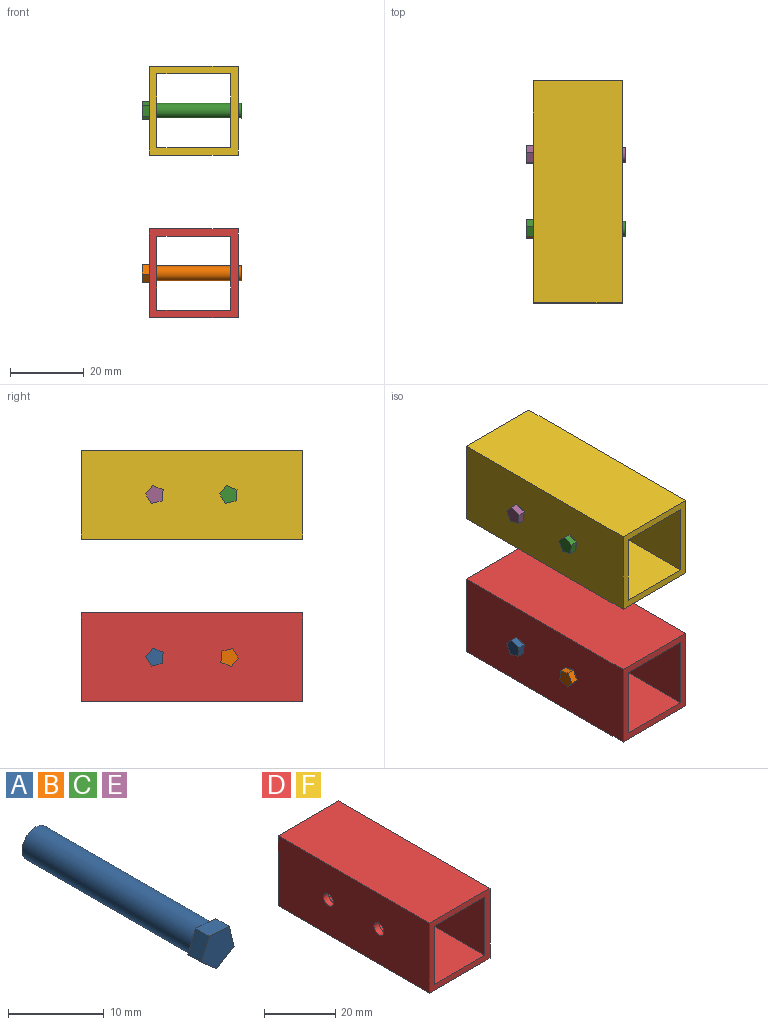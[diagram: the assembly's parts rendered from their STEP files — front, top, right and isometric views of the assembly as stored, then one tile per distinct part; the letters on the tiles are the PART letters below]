
ASSEMBLY  parts=6 mates=5
PART A: 9 faces, bbox 4.8x27x4.7 mm
  f0: plane 2.92x2mm, normal (0.97,0,0.23), area 6mm2, adj f1,f4,f5,f6
  f1: plane 2.99x2mm, normal (0.08,0,1), area 6mm2, adj f0,f2,f5,f6
  f2: plane 2.77x2mm, normal (-0.92,0,0.39), area 6mm2, adj f1,f3,f5,f6
  f3: plane 2.27x2mm, normal (-0.65,0,-0.76), area 6mm2, adj f2,f4,f5,f6
  f4: plane 2.56x2mm, normal (0.52,0,-0.85), area 6mm2, adj f0,f3,f5,f6
  f5: plane 4.84x4.72mm, normal (0,-1,0), area 15.5mm2, adj f0,f1,f2,f3,f4
  f6: plane 4.84x4.72mm, normal (0,1,0), area 2.9mm2, adj f0,f1,f2,f3,f4,f7
  f7: cylinder r=2mm len=25mm, axis (0,-1,0), area 314.2mm2, adj f6,f8
  f8: plane 4x4mm, normal (0,1,0), area 12.6mm2, adj f7
PART B: same geometry as A
PART C: same geometry as A
PART D: 14 faces, bbox 24x60x24 mm
  f0: plane 60x20mm, normal (0,0,1), area 1200mm2, adj f1,f7,f8,f9
  f1: plane 60x20mm, normal (1,0,0), area 1174.9mm2, adj f0,f2,f8,f9,f12,f13
  f2: plane 60x20mm, normal (0,0,-1), area 1200mm2, adj f1,f7,f8,f9
  f3: plane 60x24mm, normal (0,0,1), area 1440mm2, adj f4,f6,f8,f9
  f4: plane 60x24mm, normal (-1,0,0), area 1414.9mm2, adj f3,f5,f8,f9,f12,f13
  f5: plane 60x24mm, normal (0,0,-1), area 1440mm2, adj f4,f6,f8,f9
  f6: plane 60x24mm, normal (1,0,0), area 1414.9mm2, adj f3,f5,f8,f9,f10,f11
  f7: plane 60x20mm, normal (-1,0,0), area 1174.9mm2, adj f0,f2,f8,f9,f10,f11
  f8: plane 24x24mm, normal (0,-1,0), area 176mm2, adj f0,f1,f2,f3,f4,f5,f6,f7
  f9: plane 24x24mm, normal (0,1,0), area 176mm2, adj f0,f1,f2,f3,f4,f5,f6,f7
  f10: cylinder r=2mm len=4mm, axis (1,0,0), area 25.1mm2, adj f6,f7
  f11: cylinder r=2mm len=4mm, axis (1,0,0), area 25.1mm2, adj f6,f7
  f12: cylinder r=2mm len=4mm, axis (1,0,0), area 25.1mm2, adj f1,f4
  f13: cylinder r=2mm len=4mm, axis (1,0,0), area 25.1mm2, adj f1,f4
PART E: same geometry as A
PART F: same geometry as D
PLACE A rot(axis=(0.58,0.58,-0.58),120deg) t=(15.78,22.93,-115.73)mm
PLACE B rot(axis=(-0.58,-0.58,-0.58),120deg) t=(15.78,-57.84,-56.26)mm
PLACE C rot(axis=(0.58,0.58,-0.58),120deg) t=(15.78,2.93,-71.73)mm
PLACE D t=(32.46,12.55,-75.25)mm fixed
PLACE E rot(axis=(0.58,0.58,-0.58),120deg) t=(15.78,22.93,-71.73)mm
PLACE F rot(axis=(1,0,0),180deg) t=(32.46,-47.45,-52.75)mm
MATE fastened C.f7 <-> F.f10  axis (1,0,0) through (15.78,-27.45,-42)mm
MATE fastened E.f7 <-> F.f11  axis (1,0,0) through (15.78,-7.45,-42)mm
MATE fastened A.f7 <-> D.f10  axis (1,0,0) through (15.78,-7.45,-86)mm
MATE parallel F.f3 <-> D.f3  axis (0,0,-1) through (27.78,-17.45,-54)mm
MATE fastened B.f7 <-> D.f11  axis (1,0,0) through (15.78,-27.45,-86)mm
